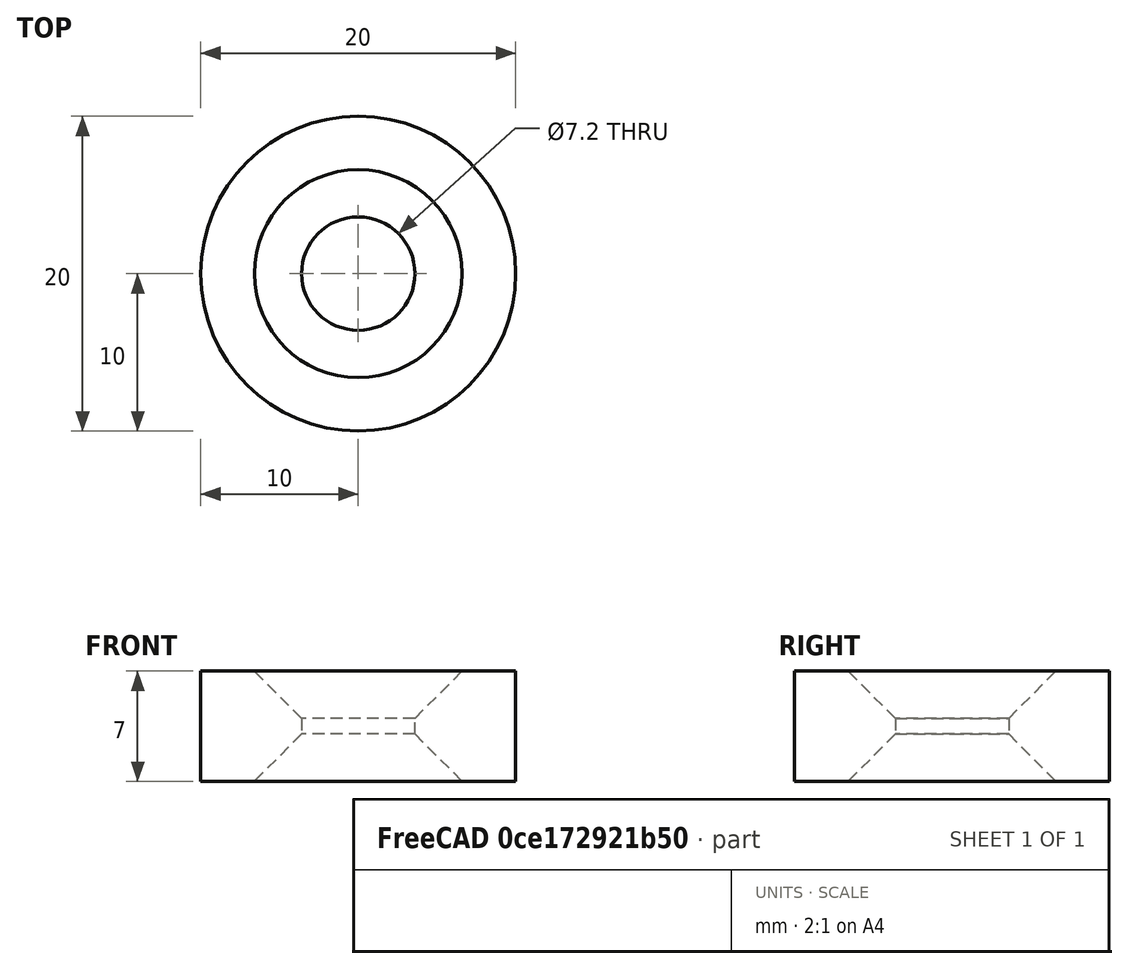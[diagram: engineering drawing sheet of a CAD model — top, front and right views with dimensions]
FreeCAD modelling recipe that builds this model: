
FCSTD DOCUMENT  (FreeCAD 1.0R39109 (Git))
Label: bearing center
License: All rights reserved
objects: Sketcher::SketchObject×1, PartDesign::Pad×1, PartDesign::Chamfer×1, PartDesign::Body×1
note: 9 computed .brp shape members not serialized (recipe doc carries the construction recipe); baked Part::Feature solids carry a one-line shape summary decoded from their .brp

FEATURE [Sketcher::SketchObject] Sketch
  ArcFitTolerance = 1e-06
  AttachmentSupport = -> [XY_Plane]
  FullyConstrained = true
  MakeInternals = false
  MapMode = 5
  sketch-geometry (2):
    g0: Circle CenterX=0 CenterY=0 CenterZ=0 NormalX=0 NormalY=0 NormalZ=1 AngleXU=0 Radius=10
    g1: Circle CenterX=0 CenterY=0 CenterZ=0 NormalX=0 NormalY=0 NormalZ=1 AngleXU=0 Radius=3.6
  constraints (4):
    c: Coincident(g0,g-1)
    c: Radius(g0) = 10
    c: Coincident(g1,g0)
    c: Radius(g1) = 3.6
FEATURE [PartDesign::Pad] Pad
  Direction = (0,0,1)
  Length = 7
  Length2 = 10
  Profile = -> Sketch
  ReferenceAxis = -> Sketch [N_Axis]
  Refine = true
  Suppressed = false
  Type = 0
FEATURE [PartDesign::Chamfer] Chamfer
  Angle = 45
  Base = -> Pad [Edge6,Edge5]
  BaseFeature = -> Pad
  ChamferType = 0
  FlipDirection = false
  Refine = true
  Size = 3
  Size2 = 1
  SupportTransform = false
  Suppressed = false
  UseAllEdges = false
FEATURE [PartDesign::Body] Body
  AllowCompound = false
  Group = -> [Sketch,Pad,Chamfer]
  Origin = -> Origin
  Tip = -> Chamfer
